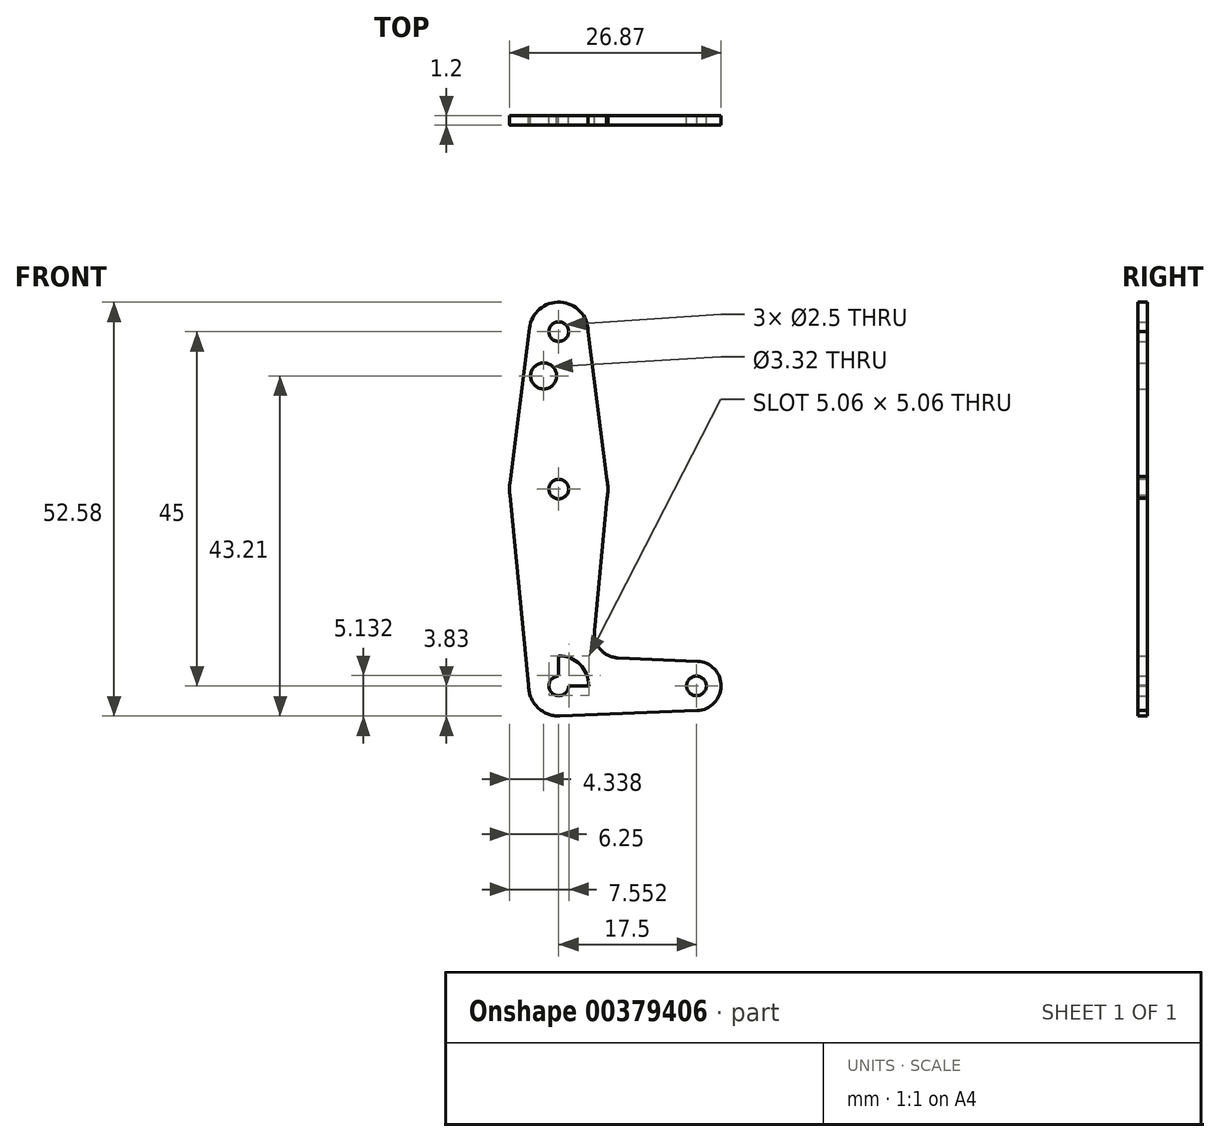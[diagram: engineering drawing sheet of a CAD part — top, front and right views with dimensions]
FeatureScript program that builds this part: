
annotation { "Feature Type Name" : "Feature", "Feature Type Description" : "" }
export const myFeature = defineFeature(function(context is Context, id is Id, definition is map)
    precondition{}
    {
        {
            var Q0;
            Q0=qCreatedBy(makeId("Front.planeOp"),FACE);
            var sketch = newSketch(context, id + "F0", { "sketchPlane" : qUnion([Q0])});
            skLineSegment(sketch, "E0", {"start": v(0, 0) * mm, "end": v(0, 45) * mm});
            skLineSegment(sketch, "E1", {"start": v(0, 45) * mm, "end": v(0, 0) * mm});
            skLineSegment(sketch, "E2", {"start": v(0, 0) * mm, "end": v(17.5, 0) * mm});
            skLineSegment(sketch, "E3", {"start": v(17.5, 0) * mm, "end": v(0, 0) * mm});
            skLineSegment(sketch, "E4", {"start": v(0, 25) * mm, "end": v(0, 45) * mm});
            skCircle(sketch, "E5", {"center": v(0, 45) * mm, "radius": 3.75 * mm});
            skCircle(sketch, "E6", {"center": v(0, 25) * mm, "radius": 6.25 * mm});
            skCircle(sketch, "E7", {"center": v(17.5, 0) * mm, "radius": 3.12 * mm});
            skLineSegment(sketch, "E8", {"start": v(0, 25) * mm, "end": v(0, 0) * mm});
            skLineSegment(sketch, "E9", {"start": v(3.75, 45.02) * mm, "end": v(6.25, 24.94) * mm});
            skLineSegment(sketch, "E10", {"start": v(4.55, 6.98) * mm, "end": v(6.25, 24.94) * mm});
            skLineSegment(sketch, "E11", {"start": v(7.53, 3.56) * mm, "end": v(17.64, 3.12) * mm});
            skCircle(sketch, "E12", {"center": v(0, 45) * mm, "radius": 1.25 * mm});
            skCircle(sketch, "E13", {"center": v(0, 25) * mm, "radius": 1.25 * mm});
            skCircle(sketch, "E14", {"center": v(0, 0) * mm, "radius": 1.25 * mm});
            skCircle(sketch, "E15", {"center": v(17.5, 0) * mm, "radius": 1.25 * mm});
            skCircle(sketch, "E16", {"center": v(-1.91, 39.38) * mm, "radius": 1.66 * mm});
            skLineSegment(sketch, "E17", {"start": v(-1.91, 39.38) * mm, "end": v(0, 39.38) * mm});
            skLineSegment(sketch, "E18", {"start": v(0, 25) * mm, "end": v(0, 39.38) * mm});
            skArc(sketch, "E19.filletArc", {"start": v(4.55, 6.98) * mm, "mid": v(5.3, 4.63) * mm, "end": v(7.53, 3.56) * mm});
            skCircle(sketch, "E20", {"center": v(0, 0) * mm, "radius": 3.83 * mm});
            skLineSegment(sketch, "E21", {"start": v(17.6, -3.12) * mm, "end": v(0, -3.83) * mm});
            skLineSegment(sketch, "E22", {"start": v(-3.72, 45.44) * mm, "end": v(-6.2, 25.78) * mm});
            skLineSegment(sketch, "E23", {"start": v(-6.23, 24.55) * mm, "end": v(-3.73, -0.87) * mm});
            skSolve(sketch);
        }
        {
            var Q0;
            Q0 = qSketchRegion(id + "F0", true);
            var Q1;
            {var subQ0=sQuery(id+"F0.wireOp",EDGE,"E20");var subQ1=sQuery(id+"F0.wireOp",EDGE,"E3");var subQ2=makeQuery(id+"F0.imprint","INTERSECT",VERTEX,{"derivedFrom":[subQ1,subQ0]});Q1=makeQuery(id+"F0.imprint","IMPRINT",FACE,{"disambiguationData":[TD([[makeQuery(id+"F0.imprint","IMPRINT",EDGE,{"disambiguationData":[TD([[subQ2,-1.0]])],"derivedFrom":subQ1}),-1.0]])]});}
            extrude(context, id + "F1", {"entities" : qUnion([Q0, Q1]), "depth" : 1.2 * mm});
        }
    });
